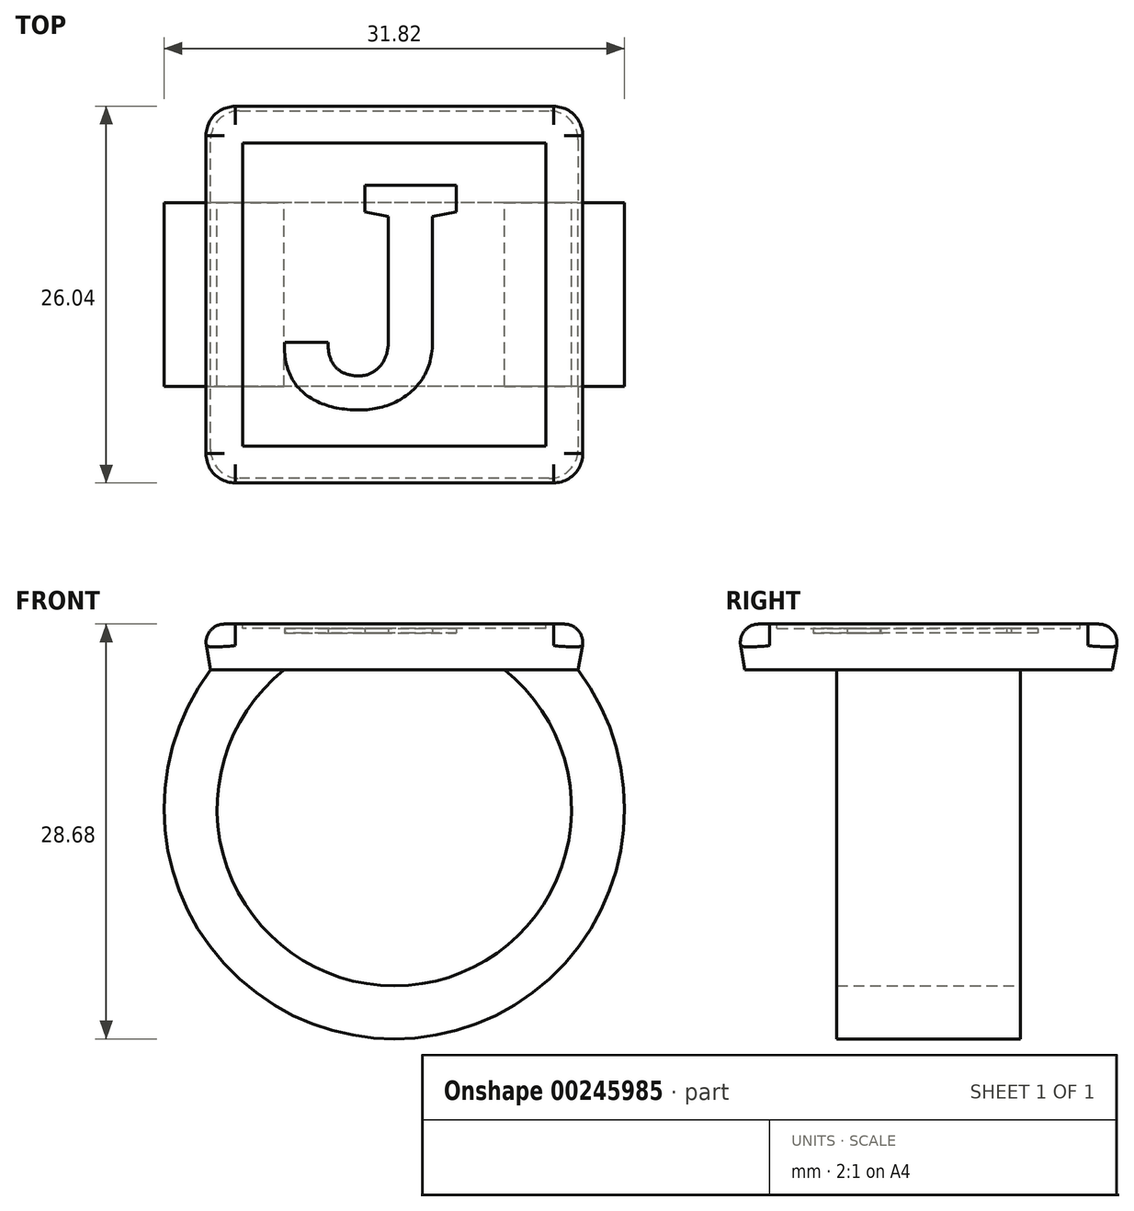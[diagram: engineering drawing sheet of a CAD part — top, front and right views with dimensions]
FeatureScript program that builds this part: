
annotation { "Feature Type Name" : "Feature", "Feature Type Description" : "" }
export const myFeature = defineFeature(function(context is Context, id is Id, definition is map)
    precondition{}
    {
        {
            var Q0;
            Q0=qCreatedBy(makeId("Top.planeOp"),FACE);
            var sketch = newSketch(context, id + "F0", { "sketchPlane" : qUnion([Q0])});
            skLineSegment(sketch, "E0.bottom", {"start": v(12.7, 12.7) * mm, "end": v(-12.7, 12.7) * mm});
            skLineSegment(sketch, "E0.top", {"start": v(12.7, -12.7) * mm, "end": v(-12.7, -12.7) * mm});
            skLineSegment(sketch, "E0.left", {"start": v(12.7, 12.7) * mm, "end": v(12.7, -12.7) * mm});
            skLineSegment(sketch, "E0.right", {"start": v(-12.7, 12.7) * mm, "end": v(-12.7, -12.7) * mm});
            skPoint(sketch, "E0.middle", {"position": v(0, 0) * mm});
            skSolve(sketch);
        }
        {
            var Q0;
            Q0=makeQuery(id+"F0.imprint","IMPRINT",FACE,{"disambiguationData":[TD([[makeQuery(id+"F0.imprint","IMPRINT",EDGE,{"derivedFrom":sQuery(id+"F0.wireOp",EDGE,"E0.bottom")}),1.0]])]});
            extrude(context, id + "F1", {"entities" : qUnion([Q0]), "depth" : 3.17 * mm, "hasDraft" : true, "draftAngle" : 10 * degree});
        }
        {
            var Q0;
            Q0=qCreatedBy(makeId("Front.planeOp"),FACE);
            var sketch = newSketch(context, id + "F2", { "sketchPlane" : qUnion([Q0])});
            skArc(sketch, "E1", {"start": v(-10.16, 0) * mm, "mid": v(0, -23.56) * mm, "end": v(10.16, 0) * mm});
            skSolve(sketch);
        }
        {
            var Q0;
            Q0=qCreatedBy(makeId("Top.planeOp"),FACE);
            var sketch = newSketch(context, id + "F3", { "sketchPlane" : qUnion([Q0])});
            skLineSegment(sketch, "E2.bottom", {"start": v(12.7, -6.35) * mm, "end": v(7.62, -6.35) * mm});
            skLineSegment(sketch, "E2.top", {"start": v(12.7, 6.35) * mm, "end": v(7.62, 6.35) * mm});
            skLineSegment(sketch, "E2.left", {"start": v(12.7, -6.35) * mm, "end": v(12.7, 6.35) * mm});
            skLineSegment(sketch, "E2.right", {"start": v(7.62, -6.35) * mm, "end": v(7.62, 6.35) * mm});
            skPoint(sketch, "E2.middle", {"position": v(10.16, 0) * mm});
            skSolve(sketch);
        }
        {
            var Q0;
            Q0 = qSketchRegion(id + "F3", true);
            var Q1;
            Q1 = qConstructionFilter(qBodyType(qCreatedBy(id + "F2" ,EDGE), BodyType.WIRE), ConstructionObject.NO);
            sweep(context, id + "F4", {"operationType" : NewBodyOperationType.ADD, "profiles" : qUnion([Q0]), "path" : qUnion([Q1])});
        }
        {
            var Q0;
            Q0=qCreatedBy(makeId("Front.planeOp"),FACE);
            var sketch = newSketch(context, id + "F5", { "sketchPlane" : qUnion([Q0])});
            skLineSegment(sketch, "E3.0", {"start": v(-7.62, 0) * mm, "end": v(-10.16, 0) * mm});
            skLineSegment(sketch, "E4.0", {"start": v(-10.16, 0) * mm, "end": v(-10.01, -2.54) * mm});
            skArc(sketch, "E5", {"start": v(-7.62, 0) * mm, "mid": v(-8.9, -1.18) * mm, "end": v(-10.01, -2.54) * mm});
            skPoint(sketch, "E6.orphan", {"position": v(12.7, 0) * mm});
            skPoint(sketch, "E7.orphan", {"position": v(-12.7, 0) * mm});
            skSolve(sketch);
        }
        {
            var Q0;
            {var subQ0=sQuery(id+"F5.wireOp",EDGE,"E4.0");Q0=makeQuery(id+"F5.imprint","IMPRINT",FACE,{"disambiguationData":[TD([[makeQuery(id+"F5.imprint","IMPRINT",EDGE,{"derivedFrom":subQ0}),1.0]])]});}
            extrude(context, id + "F6", {"entities" : qUnion([Q0]), "operationType" : NewBodyOperationType.ADD, "endBound" : BoundingType.SYMMETRIC, "depth" : 12.7 * mm});
        }
        {
            var Q0;
            Q0=makeQuery(id+"F1.opExtrude","SWEPT_EDGE",EDGE,{"disambiguationData":[OSD([sQuery(id+"F0.wireOp",EDGE,"E0.bottom"),sQuery(id+"F0.wireOp",EDGE,"E0.right")])]});
            var Q1;
            Q1=makeQuery(id+"F1.opExtrude","SWEPT_EDGE",EDGE,{"disambiguationData":[OSD([sQuery(id+"F0.wireOp",EDGE,"E0.top"),sQuery(id+"F0.wireOp",EDGE,"E0.right")])]});
            var Q2;
            Q2=makeQuery(id+"F1.opExtrude","SWEPT_EDGE",EDGE,{"disambiguationData":[OSD([sQuery(id+"F0.wireOp",EDGE,"E0.bottom"),sQuery(id+"F0.wireOp",EDGE,"E0.left")])]});
            var Q3;
            Q3=makeQuery(id+"F1.opExtrude","SWEPT_EDGE",EDGE,{"disambiguationData":[OSD([sQuery(id+"F0.wireOp",EDGE,"E0.top"),sQuery(id+"F0.wireOp",EDGE,"E0.left")])]});
            fillet(context, id + "F7", {"entities" : qUnion([Q0, Q1, Q2, Q3]), "radius" : 2.03 * mm, "tangentPropagation" : true, "allowEdgeOverflow" : false});
        }
        {
            var Q0;
            Q0=makeQuery(id+"F1.opExtrude","CAP_EDGE",EDGE,{"disambiguationData":[OSD([sQuery(id+"F0.wireOp",EDGE,"E0.bottom")])],"isStart":false});
            var Q1;
            Q1=makeQuery(id+"F1.opExtrude","CAP_EDGE",EDGE,{"disambiguationData":[OSD([sQuery(id+"F0.wireOp",EDGE,"E0.right")])],"isStart":false});
            var Q2;
            Q2=makeQuery(id+"F1.opExtrude","CAP_EDGE",EDGE,{"disambiguationData":[OSD([sQuery(id+"F0.wireOp",EDGE,"E0.top")])],"isStart":false});
            var Q3;
            Q3=makeQuery(id+"F1.opExtrude","CAP_EDGE",EDGE,{"disambiguationData":[OSD([sQuery(id+"F0.wireOp",EDGE,"E0.left")])],"isStart":false});
            fillet(context, id + "F8", {"entities" : qUnion([Q0, Q1, Q2, Q3]), "radius" : 1.27 * mm, "tangentPropagation" : true, "allowEdgeOverflow" : false});
        }
        {
            var Q0;
            Q0=makeQuery(id+"F1.opExtrude","CAP_FACE",FACE,{"disambiguationData":[OSD([sQuery(id+"F0.wireOp",EDGE,"E0.bottom"),sQuery(id+"F0.wireOp",EDGE,"E0.top"),sQuery(id+"F0.wireOp",EDGE,"E0.left"),sQuery(id+"F0.wireOp",EDGE,"E0.right")])],"isStart":false});
            var sketch = newSketch(context, id + "F9", { "sketchPlane" : qUnion([Q0])});
            skLineSegment(sketch, "E8.0", {"start": v(10.48, 10.48) * mm, "end": v(-10.48, 10.48) * mm});
            skLineSegment(sketch, "E8.1", {"start": v(10.48, -10.48) * mm, "end": v(10.48, 10.48) * mm});
            skLineSegment(sketch, "E8.2", {"start": v(-10.48, -10.48) * mm, "end": v(10.48, -10.48) * mm});
            skLineSegment(sketch, "E8.3", {"start": v(-10.48, 10.48) * mm, "end": v(-10.48, -10.48) * mm});
            skSolve(sketch);
        }
        {
            var Q0;
            Q0=makeQuery(id+"F9.imprint","IMPRINT",FACE,{"disambiguationData":[TD([[makeQuery(id+"F9.imprint","IMPRINT",EDGE,{"derivedFrom":sQuery(id+"F9.wireOp",EDGE,"E8.0")}),1.0]])]});
            extrude(context, id + "F10", {"entities" : qUnion([Q0]), "operationType" : NewBodyOperationType.REMOVE, "oppositeDirection" : true, "depth" : 0.64 * mm});
        }
        {
            var Q0;
            Q0=makeQuery(id+"F10.boolean.opBoolean","COPY",FACE,{"derivedFrom":makeQuery(id+"F10.opExtrude","CAP_FACE",FACE,{"disambiguationData":[OSD([sQuery(id+"F9.wireOp",EDGE,"E8.0"),sQuery(id+"F9.wireOp",EDGE,"E8.1"),sQuery(id+"F9.wireOp",EDGE,"E8.2"),sQuery(id+"F9.wireOp",EDGE,"E8.3")])],"isStart":false})});
            var sketch = newSketch(context, id + "F11", { "sketchPlane" : qUnion([Q0])});
            skText(sketch, "E9", { "text": "J", "fontName": "RobotoSlab-Bold.ttf"});
            const initialGuessF11  = {"E9": [-0.00796, -0.00775, 1, 0, 0.0155]};
            skSetInitialGuess(sketch, initialGuessF11);
            skSolve(sketch);
        }
        {
            var Q0;
            Q0=makeQuery(id+"F11.imprint","IMPRINT",FACE,{"disambiguationData":[TD([[makeQuery(id+"F11.imprint","IMPRINT",EDGE,{"derivedFrom":sQuery(id+"F11.wireOp",EDGE,"E9.sketch_text.stroke-0")}),1.0]])]});
            extrude(context, id + "F12", {"entities" : qUnion([Q0]), "operationType" : NewBodyOperationType.ADD, "depth" : 0.32 * mm});
        }
    });
